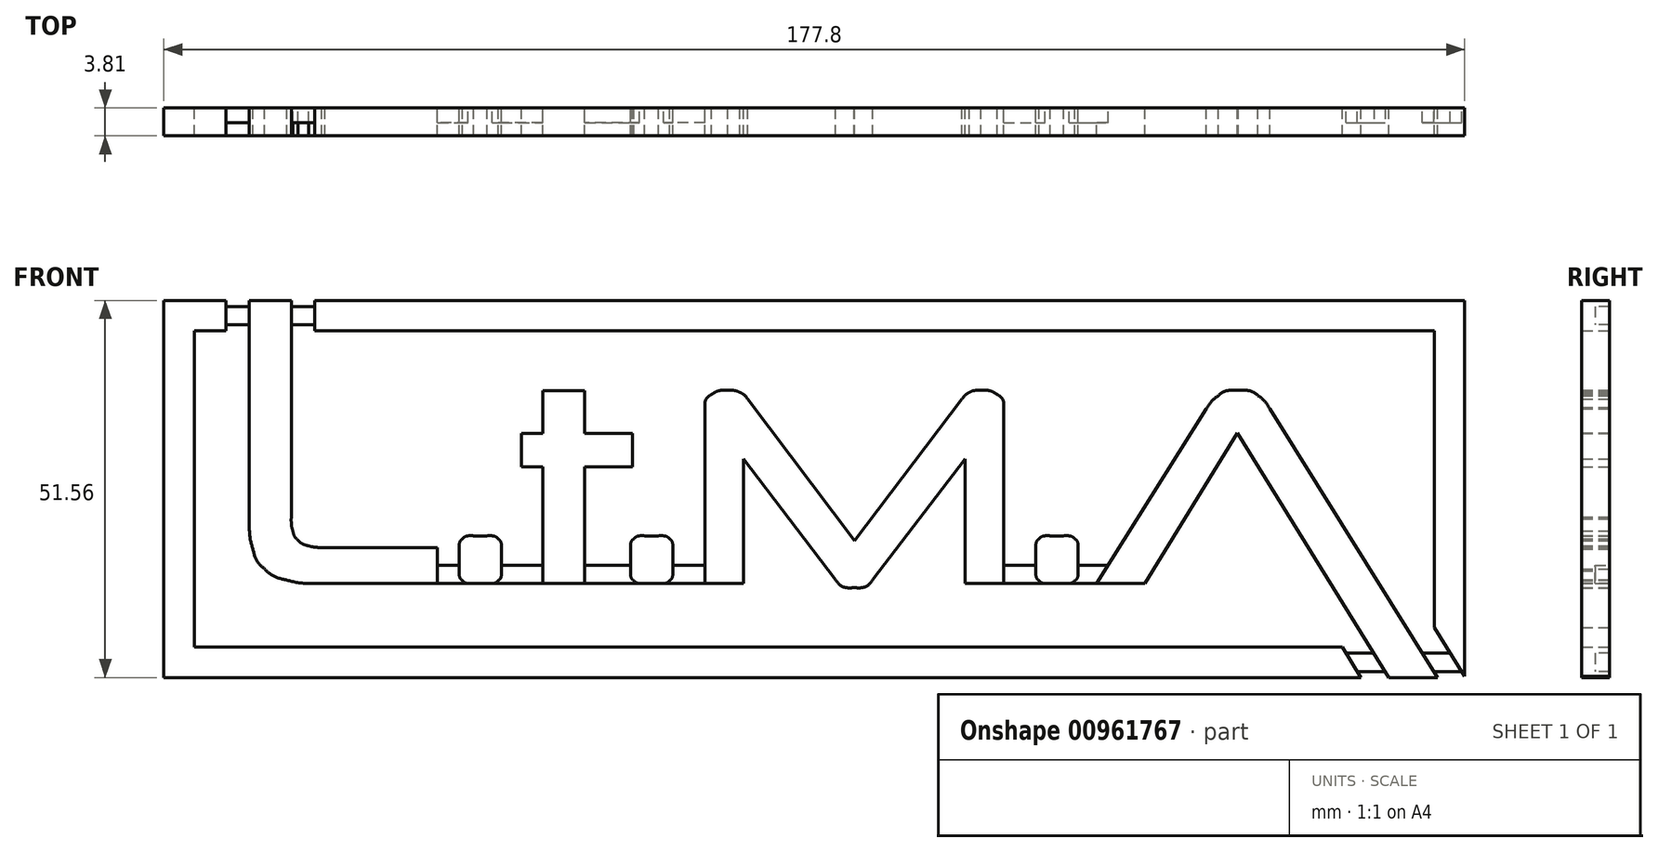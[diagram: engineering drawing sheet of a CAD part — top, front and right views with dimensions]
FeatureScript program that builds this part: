
annotation { "Feature Type Name" : "Feature", "Feature Type Description" : "" }
export const myFeature = defineFeature(function(context is Context, id is Id, definition is map)
    precondition{}
    {
        {
            var Q0;
            Q0=qCreatedBy(makeId("Front.planeOp"),FACE);
            var sketch = newSketch(context, id + "F0", { "sketchPlane" : qUnion([Q0])});
            skLineSegment(sketch, "E0", {"start": v(-214.36, -101.22) * mm, "end": v(-214.36, -131.05) * mm});
            skLineSegment(sketch, "E1", {"start": v(-204.51, -139.92) * mm, "end": v(-188.67, -139.92) * mm});
            skLineSegment(sketch, "E2", {"start": v(-188.67, -139.92) * mm, "end": v(-188.67, -135) * mm});
            skLineSegment(sketch, "E3", {"start": v(-188.67, -135) * mm, "end": v(-204.02, -135) * mm});
            skLineSegment(sketch, "E4", {"start": v(-208.64, -130.83) * mm, "end": v(-208.64, -101.22) * mm});
            skLineSegment(sketch, "E5", {"start": v(-208.64, -101.22) * mm, "end": v(-214.36, -101.22) * mm});
            skLineSegment(sketch, "E6", {"start": v(-185.68, -135.1) * mm, "end": v(-185.68, -138.22) * mm});
            skLineSegment(sketch, "E7", {"start": v(-183.75, -139.92) * mm, "end": v(-181.9, -139.92) * mm});
            skLineSegment(sketch, "E8", {"start": v(-179.92, -138.22) * mm, "end": v(-179.92, -135.1) * mm});
            skLineSegment(sketch, "E9", {"start": v(-181.9, -133.4) * mm, "end": v(-183.75, -133.4) * mm});
            skLineSegment(sketch, "E10", {"start": v(-174.27, -113.59) * mm, "end": v(-174.27, -119.38) * mm});
            skLineSegment(sketch, "E11", {"start": v(-174.27, -119.38) * mm, "end": v(-177.15, -119.38) * mm});
            skLineSegment(sketch, "E12", {"start": v(-177.15, -119.38) * mm, "end": v(-177.15, -123.97) * mm});
            skLineSegment(sketch, "E13", {"start": v(-177.15, -123.97) * mm, "end": v(-174.27, -123.97) * mm});
            skLineSegment(sketch, "E14", {"start": v(-174.27, -123.97) * mm, "end": v(-174.27, -139.92) * mm});
            skLineSegment(sketch, "E15", {"start": v(-174.27, -139.92) * mm, "end": v(-168.51, -139.92) * mm});
            skLineSegment(sketch, "E16", {"start": v(-168.51, -139.92) * mm, "end": v(-168.51, -123.97) * mm});
            skLineSegment(sketch, "E17", {"start": v(-168.51, -123.97) * mm, "end": v(-162.04, -123.97) * mm});
            skLineSegment(sketch, "E18", {"start": v(-162.04, -123.97) * mm, "end": v(-162.04, -119.38) * mm});
            skLineSegment(sketch, "E19", {"start": v(-162.04, -119.38) * mm, "end": v(-168.51, -119.38) * mm});
            skLineSegment(sketch, "E20", {"start": v(-168.51, -119.38) * mm, "end": v(-168.51, -113.59) * mm});
            skLineSegment(sketch, "E21", {"start": v(-168.51, -113.59) * mm, "end": v(-174.27, -113.59) * mm});
            skLineSegment(sketch, "E22", {"start": v(-162.26, -135.1) * mm, "end": v(-162.26, -138.22) * mm});
            skLineSegment(sketch, "E23", {"start": v(-160.33, -139.92) * mm, "end": v(-158.47, -139.92) * mm});
            skLineSegment(sketch, "E24", {"start": v(-156.5, -138.22) * mm, "end": v(-156.5, -135.1) * mm});
            skLineSegment(sketch, "E25", {"start": v(-158.47, -133.4) * mm, "end": v(-160.33, -133.4) * mm});
            skLineSegment(sketch, "E26", {"start": v(-116.98, -114.72) * mm, "end": v(-131.67, -134.09) * mm});
            skLineSegment(sketch, "E27", {"start": v(-131.67, -134.09) * mm, "end": v(-146.24, -114.72) * mm});
            skLineSegment(sketch, "E28", {"start": v(-152.07, -115.86) * mm, "end": v(-152.07, -139.92) * mm});
            skLineSegment(sketch, "E29", {"start": v(-152.07, -139.92) * mm, "end": v(-146.8, -139.92) * mm});
            skLineSegment(sketch, "E30", {"start": v(-146.8, -139.92) * mm, "end": v(-146.8, -122.9) * mm});
            skLineSegment(sketch, "E31", {"start": v(-146.8, -122.9) * mm, "end": v(-134.24, -139.4) * mm});
            skLineSegment(sketch, "E32", {"start": v(-129.17, -139.4) * mm, "end": v(-116.57, -122.9) * mm});
            skLineSegment(sketch, "E33", {"start": v(-116.57, -122.9) * mm, "end": v(-116.57, -139.92) * mm});
            skLineSegment(sketch, "E34", {"start": v(-116.57, -139.92) * mm, "end": v(-111.3, -139.92) * mm});
            skLineSegment(sketch, "E35", {"start": v(-111.3, -139.92) * mm, "end": v(-111.3, -115.86) * mm});
            skLineSegment(sketch, "E36", {"start": v(-106.87, -135.1) * mm, "end": v(-106.87, -138.22) * mm});
            skLineSegment(sketch, "E37", {"start": v(-104.93, -139.92) * mm, "end": v(-103.08, -139.92) * mm});
            skLineSegment(sketch, "E38", {"start": v(-101.1, -138.22) * mm, "end": v(-101.1, -135.1) * mm});
            skLineSegment(sketch, "E39", {"start": v(-103.08, -133.4) * mm, "end": v(-104.93, -133.4) * mm});
            skLineSegment(sketch, "E40", {"start": v(-83.56, -116.05) * mm, "end": v(-98.57, -139.92) * mm});
            skLineSegment(sketch, "E41", {"start": v(-98.57, -139.92) * mm, "end": v(-91.94, -139.92) * mm});
            skLineSegment(sketch, "E42", {"start": v(-91.94, -139.92) * mm, "end": v(-79.32, -119.35) * mm});
            skLineSegment(sketch, "E43", {"start": v(-79.32, -119.35) * mm, "end": v(-58.62, -152.78) * mm});
            skLineSegment(sketch, "E44", {"start": v(-58.62, -152.78) * mm, "end": v(-51.95, -152.78) * mm});
            skLineSegment(sketch, "E45", {"start": v(-51.95, -152.78) * mm, "end": v(-74.89, -116.05) * mm});
            skLineSegment(sketch, "E46", {"start": v(-205.42, -101.22) * mm, "end": v(-205.42, -105.4) * mm});
            skLineSegment(sketch, "E47", {"start": v(-205.42, -105.4) * mm, "end": v(-52.43, -105.4) * mm});
            skLineSegment(sketch, "E48", {"start": v(-52.43, -105.4) * mm, "end": v(-52.43, -145.93) * mm});
            skLineSegment(sketch, "E49", {"start": v(-52.43, -145.93) * mm, "end": v(-48.26, -152.6) * mm});
            skLineSegment(sketch, "E50", {"start": v(-48.26, -152.6) * mm, "end": v(-48.26, -101.22) * mm});
            skLineSegment(sketch, "E51", {"start": v(-48.26, -101.22) * mm, "end": v(-205.42, -101.22) * mm});
            skLineSegment(sketch, "E52", {"start": v(-226.06, -101.22) * mm, "end": v(-226.06, -152.78) * mm});
            skLineSegment(sketch, "E53", {"start": v(-226.06, -152.78) * mm, "end": v(-62.4, -152.78) * mm});
            skLineSegment(sketch, "E54", {"start": v(-62.4, -152.78) * mm, "end": v(-65, -148.6) * mm});
            skLineSegment(sketch, "E55", {"start": v(-65, -148.6) * mm, "end": v(-221.89, -148.6) * mm});
            skLineSegment(sketch, "E56", {"start": v(-221.89, -148.6) * mm, "end": v(-221.89, -105.4) * mm});
            skLineSegment(sketch, "E57", {"start": v(-221.89, -105.4) * mm, "end": v(-217.59, -105.4) * mm});
            skLineSegment(sketch, "E58", {"start": v(-217.59, -105.4) * mm, "end": v(-217.59, -101.22) * mm});
            skLineSegment(sketch, "E59", {"start": v(-217.59, -101.22) * mm, "end": v(-226.06, -101.22) * mm});
            skFitSpline(sketch, "E60", {"points": [v(-214.36, -131.05) * mm, v(-214.36, -132.7) * mm, v(-214.2, -134.08) * mm, v(-213.9, -135.2) * mm]});
            skFitSpline(sketch, "E61", {"points": [v(-213.9, -135.2) * mm, v(-213.57, -136.33) * mm, v(-213.04, -137.24) * mm, v(-212.28, -137.93) * mm]});
            skFitSpline(sketch, "E62", {"points": [v(-212.28, -137.93) * mm, v(-211.52, -138.63) * mm, v(-210.51, -139.13) * mm, v(-209.25, -139.45) * mm]});
            skFitSpline(sketch, "E63", {"points": [v(-209.25, -139.45) * mm, v(-207.98, -139.76) * mm, v(-206.4, -139.92) * mm, v(-204.51, -139.92) * mm]});
            skFitSpline(sketch, "E64", {"points": [v(-204.02, -135) * mm, v(-204.93, -135) * mm, v(-205.68, -134.92) * mm, v(-206.27, -134.77) * mm]});
            skFitSpline(sketch, "E65", {"points": [v(-206.27, -134.77) * mm, v(-206.87, -134.62) * mm, v(-207.34, -134.37) * mm, v(-207.7, -134.03) * mm]});
            skFitSpline(sketch, "E66", {"points": [v(-207.7, -134.03) * mm, v(-208.05, -133.69) * mm, v(-208.3, -133.26) * mm, v(-208.43, -132.74) * mm]});
            skFitSpline(sketch, "E67", {"points": [v(-208.43, -132.74) * mm, v(-208.57, -132.22) * mm, v(-208.64, -131.58) * mm, v(-208.64, -130.83) * mm]});
            skFitSpline(sketch, "E68", {"points": [v(-183.75, -133.4) * mm, v(-184.46, -133.4) * mm, v(-184.95, -133.54) * mm, v(-185.24, -133.82) * mm]});
            skFitSpline(sketch, "E69", {"points": [v(-185.24, -133.82) * mm, v(-185.53, -134.1) * mm, v(-185.68, -134.53) * mm, v(-185.68, -135.1) * mm]});
            skFitSpline(sketch, "E70", {"points": [v(-185.68, -138.22) * mm, v(-185.68, -138.82) * mm, v(-185.53, -139.26) * mm, v(-185.24, -139.52) * mm]});
            skFitSpline(sketch, "E71", {"points": [v(-185.24, -139.52) * mm, v(-184.95, -139.79) * mm, v(-184.46, -139.92) * mm, v(-183.75, -139.92) * mm]});
            skFitSpline(sketch, "E72", {"points": [v(-181.9, -139.92) * mm, v(-181.16, -139.92) * mm, v(-180.65, -139.79) * mm, v(-180.36, -139.52) * mm]});
            skFitSpline(sketch, "E73", {"points": [v(-180.36, -139.52) * mm, v(-180.07, -139.26) * mm, v(-179.92, -138.82) * mm, v(-179.92, -138.22) * mm]});
            skFitSpline(sketch, "E74", {"points": [v(-179.92, -135.1) * mm, v(-179.92, -134.53) * mm, v(-180.07, -134.1) * mm, v(-180.36, -133.82) * mm]});
            skFitSpline(sketch, "E75", {"points": [v(-180.36, -133.82) * mm, v(-180.65, -133.54) * mm, v(-181.16, -133.4) * mm, v(-181.9, -133.4) * mm]});
            skFitSpline(sketch, "E76", {"points": [v(-160.33, -133.4) * mm, v(-161.04, -133.4) * mm, v(-161.54, -133.54) * mm, v(-161.83, -133.82) * mm]});
            skFitSpline(sketch, "E77", {"points": [v(-161.83, -133.82) * mm, v(-162.12, -134.1) * mm, v(-162.26, -134.53) * mm, v(-162.26, -135.1) * mm]});
            skFitSpline(sketch, "E78", {"points": [v(-162.26, -138.22) * mm, v(-162.26, -138.82) * mm, v(-162.12, -139.26) * mm, v(-161.83, -139.52) * mm]});
            skFitSpline(sketch, "E79", {"points": [v(-161.83, -139.52) * mm, v(-161.54, -139.79) * mm, v(-161.04, -139.92) * mm, v(-160.33, -139.92) * mm]});
            skFitSpline(sketch, "E80", {"points": [v(-158.47, -139.92) * mm, v(-157.74, -139.92) * mm, v(-157.23, -139.79) * mm, v(-156.94, -139.52) * mm]});
            skFitSpline(sketch, "E81", {"points": [v(-156.94, -139.52) * mm, v(-156.65, -139.26) * mm, v(-156.5, -138.82) * mm, v(-156.5, -138.22) * mm]});
            skFitSpline(sketch, "E82", {"points": [v(-156.5, -135.1) * mm, v(-156.5, -134.53) * mm, v(-156.65, -134.1) * mm, v(-156.94, -133.82) * mm]});
            skFitSpline(sketch, "E83", {"points": [v(-156.94, -133.82) * mm, v(-157.23, -133.54) * mm, v(-157.74, -133.4) * mm, v(-158.47, -133.4) * mm]});
            skFitSpline(sketch, "E84", {"points": [v(-115.94, -113.8) * mm, v(-116.3, -113.98) * mm, v(-116.65, -114.3) * mm, v(-116.98, -114.72) * mm]});
            skFitSpline(sketch, "E85", {"points": [v(-146.24, -114.72) * mm, v(-146.57, -114.3) * mm, v(-146.93, -113.98) * mm, v(-147.34, -113.8) * mm]});
            skFitSpline(sketch, "E86", {"points": [v(-147.34, -113.8) * mm, v(-147.74, -113.6) * mm, v(-148.28, -113.5) * mm, v(-148.97, -113.5) * mm]});
            skFitSpline(sketch, "E87", {"points": [v(-148.97, -113.5) * mm, v(-149.85, -113.5) * mm, v(-150.59, -113.7) * mm, v(-151.18, -114.08) * mm]});
            skFitSpline(sketch, "E88", {"points": [v(-151.18, -114.08) * mm, v(-151.77, -114.46) * mm, v(-152.07, -115.05) * mm, v(-152.07, -115.86) * mm]});
            skFitSpline(sketch, "E89", {"points": [v(-134.24, -139.4) * mm, v(-133.66, -140.12) * mm, v(-132.81, -140.49) * mm, v(-131.7, -140.49) * mm]});
            skFitSpline(sketch, "E90", {"points": [v(-131.7, -140.49) * mm, v(-130.6, -140.49) * mm, v(-129.75, -140.12) * mm, v(-129.17, -139.4) * mm]});
            skFitSpline(sketch, "E91", {"points": [v(-111.3, -115.86) * mm, v(-111.3, -115.05) * mm, v(-111.6, -114.46) * mm, v(-112.19, -114.08) * mm]});
            skFitSpline(sketch, "E92", {"points": [v(-112.19, -114.08) * mm, v(-112.78, -113.7) * mm, v(-113.52, -113.5) * mm, v(-114.4, -113.5) * mm]});
            skFitSpline(sketch, "E93", {"points": [v(-114.4, -113.5) * mm, v(-115.06, -113.5) * mm, v(-115.57, -113.6) * mm, v(-115.94, -113.8) * mm]});
            skFitSpline(sketch, "E94", {"points": [v(-104.93, -133.4) * mm, v(-105.64, -133.4) * mm, v(-106.14, -133.54) * mm, v(-106.43, -133.82) * mm]});
            skFitSpline(sketch, "E95", {"points": [v(-106.43, -133.82) * mm, v(-106.72, -134.1) * mm, v(-106.87, -134.53) * mm, v(-106.87, -135.1) * mm]});
            skFitSpline(sketch, "E96", {"points": [v(-106.87, -138.22) * mm, v(-106.87, -138.82) * mm, v(-106.72, -139.26) * mm, v(-106.43, -139.52) * mm]});
            skFitSpline(sketch, "E97", {"points": [v(-106.43, -139.52) * mm, v(-106.14, -139.79) * mm, v(-105.64, -139.92) * mm, v(-104.93, -139.92) * mm]});
            skFitSpline(sketch, "E98", {"points": [v(-103.08, -139.92) * mm, v(-102.34, -139.92) * mm, v(-101.83, -139.79) * mm, v(-101.54, -139.52) * mm]});
            skFitSpline(sketch, "E99", {"points": [v(-101.54, -139.52) * mm, v(-101.25, -139.26) * mm, v(-101.1, -138.82) * mm, v(-101.1, -138.22) * mm]});
            skFitSpline(sketch, "E100", {"points": [v(-101.1, -135.1) * mm, v(-101.1, -134.53) * mm, v(-101.25, -134.1) * mm, v(-101.54, -133.82) * mm]});
            skFitSpline(sketch, "E101", {"points": [v(-101.54, -133.82) * mm, v(-101.83, -133.54) * mm, v(-102.34, -133.4) * mm, v(-103.08, -133.4) * mm]});
            skFitSpline(sketch, "E102", {"points": [v(-81.93, -114.23) * mm, v(-82.57, -114.71) * mm, v(-83.1, -115.32) * mm, v(-83.56, -116.05) * mm]});
            skFitSpline(sketch, "E103", {"points": [v(-74.89, -116.05) * mm, v(-75.34, -115.32) * mm, v(-75.88, -114.71) * mm, v(-76.52, -114.23) * mm]});
            skFitSpline(sketch, "E104", {"points": [v(-76.52, -114.23) * mm, v(-77.15, -113.75) * mm, v(-78.04, -113.5) * mm, v(-79.2, -113.5) * mm]});
            skFitSpline(sketch, "E105", {"points": [v(-79.2, -113.5) * mm, v(-80.4, -113.5) * mm, v(-81.3, -113.75) * mm, v(-81.93, -114.23) * mm]});
            skSolve(sketch);
        }
        {
            var Q0;
            Q0 = qSketchRegion(id + "F0", true);
            extrude(context, id + "F1", {"entities" : qUnion([Q0]), "depth" : 3.8 * mm, "offsetDistance" : 25.4 * mm});
        }
        {
            var Q0;
            Q0=makeQuery(id+"F0.imprint","IMPRINT",FACE,{"disambiguationData":[TD([[makeQuery(id+"F0.imprint","IMPRINT",EDGE,{"derivedFrom":sQuery(id+"F0.wireOp",EDGE,"E46")}),1.0]])]});
            var sketch = newSketch(context, id + "F2", { "sketchPlane" : qUnion([Q0])});
            skLineSegment(sketch, "E106.bottom", {"start": v(-217.59, -102.06) * mm, "end": v(-205.42, -102.06) * mm});
            skLineSegment(sketch, "E106.top", {"start": v(-217.59, -104.56) * mm, "end": v(-205.42, -104.56) * mm});
            skLineSegment(sketch, "E106.left", {"start": v(-217.59, -102.06) * mm, "end": v(-217.59, -104.56) * mm});
            skLineSegment(sketch, "E106.right", {"start": v(-205.42, -102.06) * mm, "end": v(-205.42, -104.56) * mm});
            skLineSegment(sketch, "E107", {"start": v(-64.47, -149.44) * mm, "end": v(-50.23, -149.44) * mm});
            skLineSegment(sketch, "E108", {"start": v(-62.93, -151.94) * mm, "end": v(-48.67, -151.94) * mm});
            skLineSegment(sketch, "E109", {"start": v(-64.47, -149.44) * mm, "end": v(-62.93, -151.94) * mm});
            skLineSegment(sketch, "E110", {"start": v(-50.23, -149.44) * mm, "end": v(-48.67, -151.94) * mm});
            skLineSegment(sketch, "E111", {"start": v(-183.75, -139.92) * mm, "end": v(-188.67, -139.92) * mm});
            skLineSegment(sketch, "E112", {"start": v(-188.67, -139.92) * mm, "end": v(-188.67, -137.42) * mm});
            skLineSegment(sketch, "E113", {"start": v(-188.67, -137.42) * mm, "end": v(-185.68, -137.42) * mm});
            skLineSegment(sketch, "E114", {"start": v(-185.68, -137.42) * mm, "end": v(-183.75, -139.92) * mm});
            skLineSegment(sketch, "E115", {"start": v(-174.27, -137.42) * mm, "end": v(-174.27, -139.92) * mm});
            skLineSegment(sketch, "E116", {"start": v(-174.27, -139.92) * mm, "end": v(-181.9, -139.92) * mm});
            skLineSegment(sketch, "E117", {"start": v(-181.9, -139.92) * mm, "end": v(-179.92, -137.42) * mm});
            skLineSegment(sketch, "E118", {"start": v(-179.92, -137.42) * mm, "end": v(-174.27, -137.42) * mm});
            skLineSegment(sketch, "E119", {"start": v(-168.51, -137.42) * mm, "end": v(-162.26, -137.42) * mm});
            skLineSegment(sketch, "E120", {"start": v(-162.26, -137.42) * mm, "end": v(-160.33, -139.92) * mm});
            skLineSegment(sketch, "E121", {"start": v(-160.33, -139.92) * mm, "end": v(-168.51, -139.92) * mm});
            skLineSegment(sketch, "E122", {"start": v(-168.51, -139.92) * mm, "end": v(-168.51, -137.42) * mm});
            skLineSegment(sketch, "E123", {"start": v(-152.07, -137.42) * mm, "end": v(-152.07, -139.92) * mm});
            skLineSegment(sketch, "E124", {"start": v(-152.07, -139.92) * mm, "end": v(-158.47, -139.92) * mm});
            skLineSegment(sketch, "E125", {"start": v(-158.47, -139.92) * mm, "end": v(-156.5, -137.42) * mm});
            skLineSegment(sketch, "E126", {"start": v(-152.07, -137.42) * mm, "end": v(-156.5, -137.42) * mm});
            skLineSegment(sketch, "E127", {"start": v(-111.3, -137.42) * mm, "end": v(-106.87, -137.42) * mm});
            skLineSegment(sketch, "E128", {"start": v(-111.3, -139.92) * mm, "end": v(-104, -139.92) * mm});
            skLineSegment(sketch, "E129", {"start": v(-106.87, -137.42) * mm, "end": v(-104, -139.92) * mm});
            skLineSegment(sketch, "E130", {"start": v(-103.08, -139.92) * mm, "end": v(-98.57, -139.92) * mm});
            skLineSegment(sketch, "E131", {"start": v(-103.08, -139.92) * mm, "end": v(-101.1, -137.42) * mm});
            skLineSegment(sketch, "E132", {"start": v(-101.1, -137.42) * mm, "end": v(-97, -137.42) * mm});
            skLineSegment(sketch, "E133", {"start": v(-97, -137.42) * mm, "end": v(-98.57, -139.92) * mm});
            skLineSegment(sketch, "E134", {"start": v(-111.3, -137.42) * mm, "end": v(-111.3, -139.92) * mm});
            skSolve(sketch);
        }
        {
            var Q0;
            Q0 = qSketchRegion(id + "F2", true);
            extrude(context, id + "F3", {"entities" : qUnion([Q0]), "operationType" : NewBodyOperationType.ADD, "depth" : 2 * mm, "offsetDistance" : 25 * mm});
        }
    });
